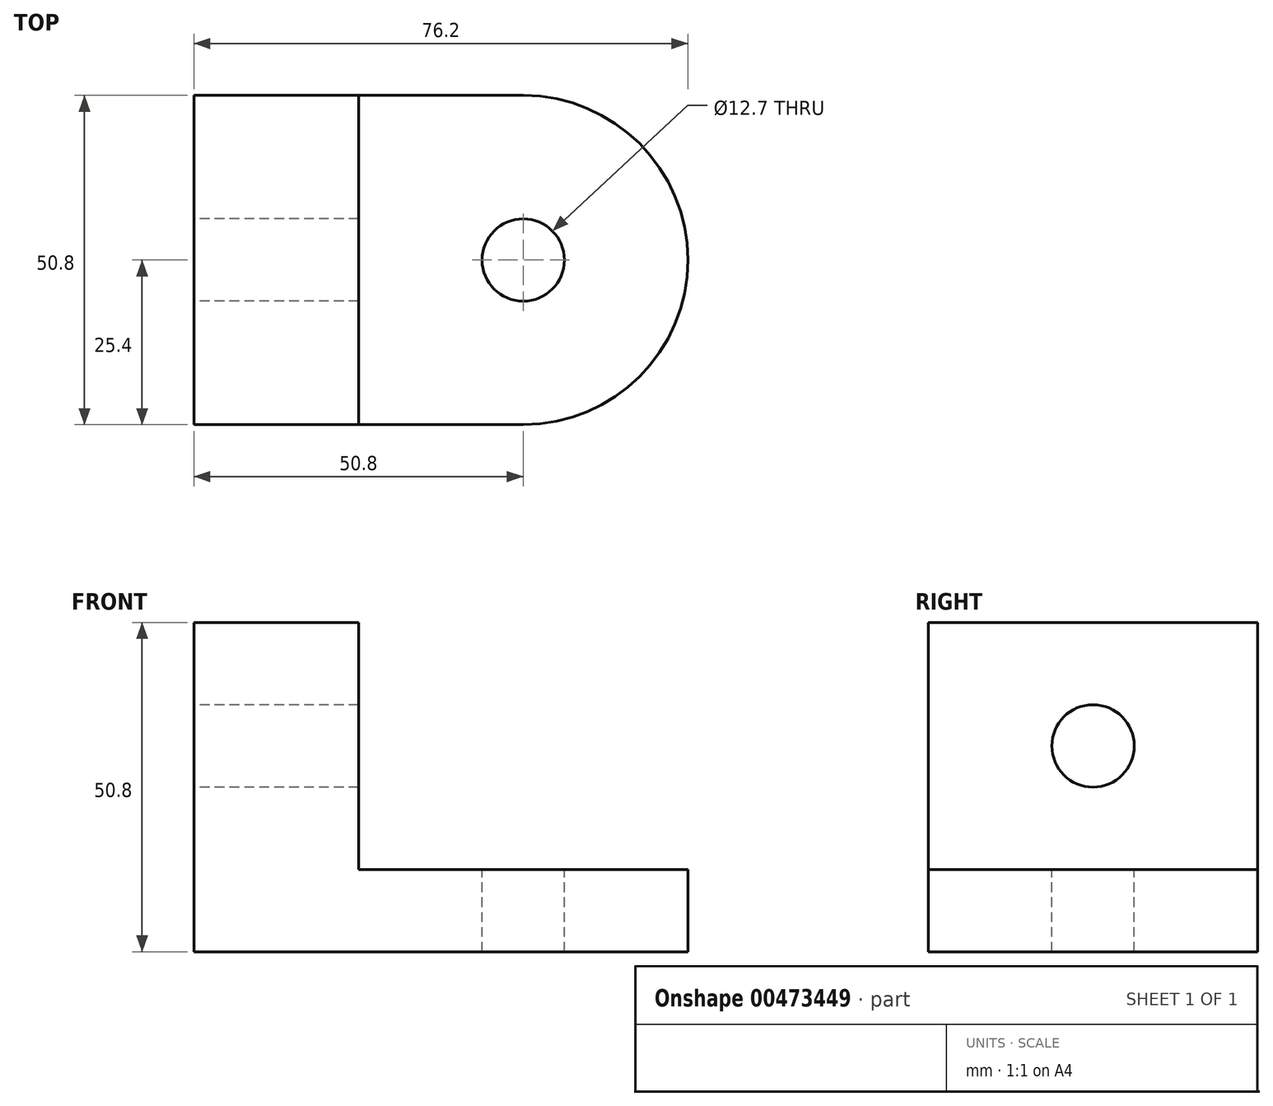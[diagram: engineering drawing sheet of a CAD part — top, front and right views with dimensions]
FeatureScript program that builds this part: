
annotation { "Feature Type Name" : "Feature", "Feature Type Description" : "" }
export const myFeature = defineFeature(function(context is Context, id is Id, definition is map)
    precondition{}
    {
        {
            var Q0;
            Q0=qCreatedBy(makeId("Right.planeOp"),FACE);
            var sketch = newSketch(context, id + "F0", { "sketchPlane" : qUnion([Q0])});
            skLineSegment(sketch, "E0", {"start": v(0, 0) * mm, "end": v(0, 38.1) * mm});
            skLineSegment(sketch, "E1", {"start": v(0, 38.1) * mm, "end": v(-50.8, 38.1) * mm});
            skLineSegment(sketch, "E2", {"start": v(-50.8, 38.1) * mm, "end": v(-50.8, 0) * mm});
            skLineSegment(sketch, "E3", {"start": v(-50.8, 0) * mm, "end": v(0, 0) * mm});
            skCircle(sketch, "E4", {"center": v(-25.4, 19.05) * mm, "radius": 6.35 * mm});
            skPoint(sketch, "E4.centerSnap0", {"position": v(-50.8, 19.05) * mm});
            skSolve(sketch);
        }
        {
            var Q0;
            Q0=makeQuery(id+"F0.imprint","IMPRINT",FACE,{"disambiguationData":[TD([[makeQuery(id+"F0.imprint","IMPRINT",EDGE,{"derivedFrom":sQuery(id+"F0.wireOp",EDGE,"E0")}),1.0]])]});
            extrude(context, id + "F1", {"entities" : qUnion([Q0]), "depth" : 25.4 * mm});
        }
        {
            var Q0;
            Q0=qCreatedBy(makeId("Top.planeOp"),FACE);
            var sketch = newSketch(context, id + "F2", { "sketchPlane" : qUnion([Q0])});
            skLineSegment(sketch, "E5", {"start": v(50.8, -50.8) * mm, "end": v(0, -50.8) * mm});
            skLineSegment(sketch, "E6", {"start": v(0, -50.8) * mm, "end": v(0, 0) * mm});
            skLineSegment(sketch, "E7", {"start": v(0, 0) * mm, "end": v(50.8, 0) * mm});
            skArc(sketch, "E8", {"start": v(50.8, -50.8) * mm, "mid": v(76.2, -25.4) * mm, "end": v(50.8, 0) * mm});
            skCircle(sketch, "E9", {"center": v(50.8, -25.4) * mm, "radius": 6.35 * mm});
            skSolve(sketch);
        }
        {
            var Q0;
            Q0 = qSketchRegion(id + "F2", true);
            extrude(context, id + "F3", {"entities" : qUnion([Q0]), "operationType" : NewBodyOperationType.ADD, "oppositeDirection" : true, "depth" : 12.7 * mm});
        }
    });
